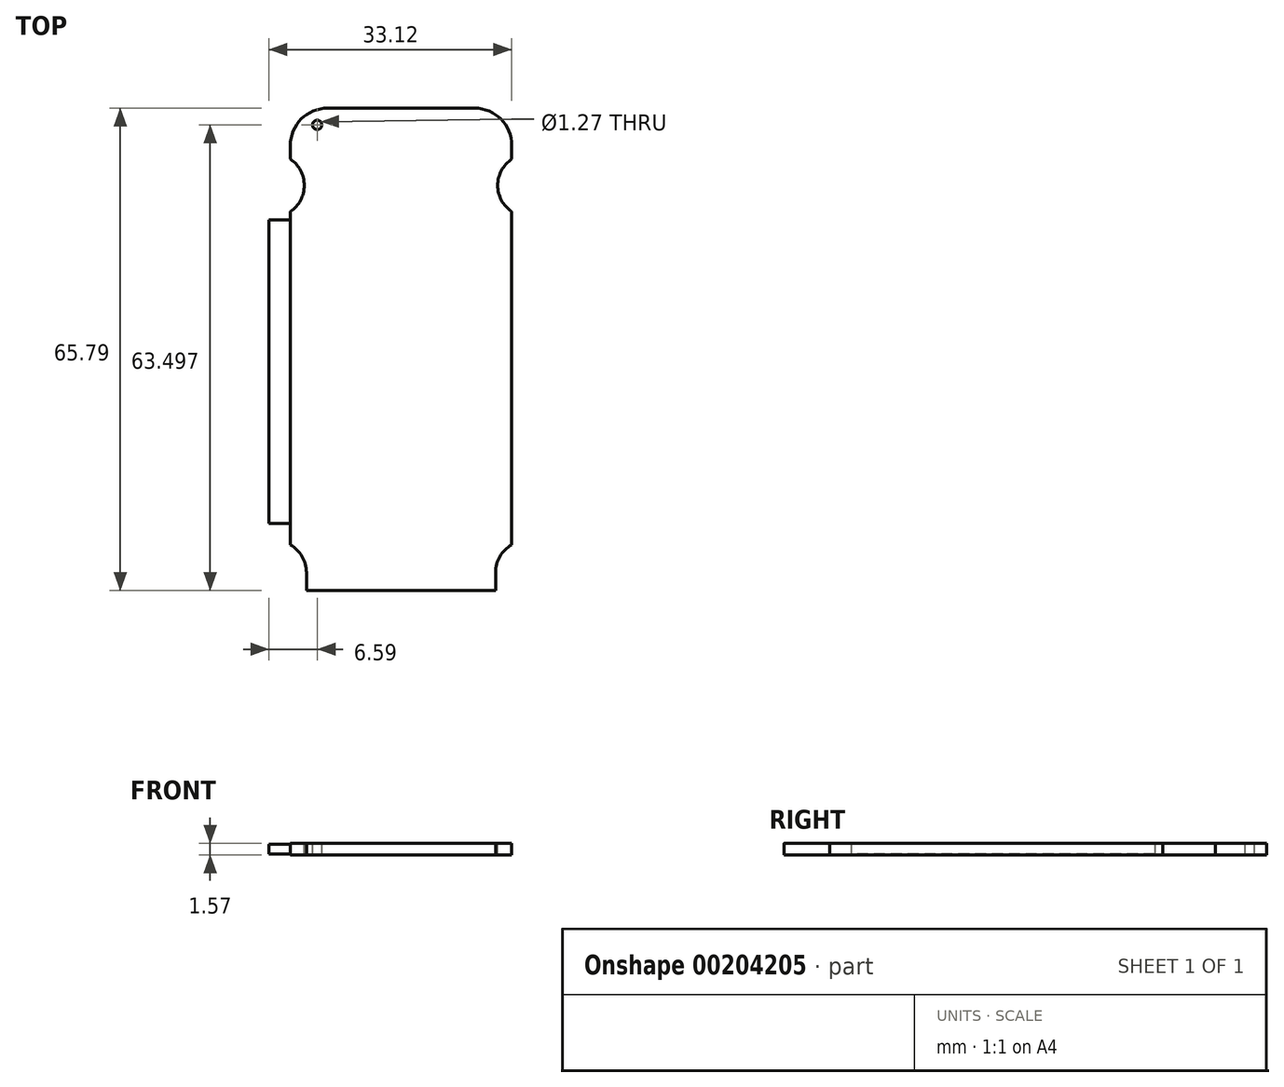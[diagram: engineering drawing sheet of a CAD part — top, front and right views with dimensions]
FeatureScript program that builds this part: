
annotation { "Feature Type Name" : "Feature", "Feature Type Description" : "" }
export const myFeature = defineFeature(function(context is Context, id is Id, definition is map)
    precondition{}
    {
        {
            var Q0;
            Q0=qCreatedBy(makeId("Top.planeOp"),FACE);
            var sketch = newSketch(context, id + "F0", { "sketchPlane" : qUnion([Q0])});
            skLineSegment(sketch, "E0.bottom", {"start": v(15.1, 28.5) * mm, "end": v(-15.1, 28.5) * mm});
            skLineSegment(sketch, "E0.top", {"start": v(15.1, -28.5) * mm, "end": v(-15.1, -28.5) * mm});
            skLineSegment(sketch, "E0.left", {"start": v(15.1, 28.5) * mm, "end": v(15.1, -28.5) * mm});
            skLineSegment(sketch, "E0.right", {"start": v(-15.1, 28.5) * mm, "end": v(-15.1, -28.5) * mm});
            skPoint(sketch, "E0.middle", {"position": v(0, 0) * mm});
            skSolve(sketch);
        }
        {
            var Q0;
            Q0=qSketchRegion(id+"F0",true);
            extrude(context, id + "F1", {"entities" : qUnion([Q0]), "depth" : 1.57 * mm});
        }
        {
            var Q0;
            Q0=makeQuery(id+"F1.opExtrude","SWEPT_FACE",FACE,{"disambiguationData":[OSD([sQuery(id+"F0.wireOp",EDGE,"E0.top")])]});
            var sketch = newSketch(context, id + "F2", { "sketchPlane" : qUnion([Q0])});
            skLineSegment(sketch, "E1.bottom", {"start": v(-15.1, 1.57) * mm, "end": v(15.1, 1.57) * mm});
            skLineSegment(sketch, "E1.top", {"start": v(-15.1, 0) * mm, "end": v(15.1, 0) * mm});
            skLineSegment(sketch, "E1.left", {"start": v(-15.1, 1.57) * mm, "end": v(-15.1, 0) * mm});
            skLineSegment(sketch, "E1.right", {"start": v(15.1, 1.57) * mm, "end": v(15.1, 0) * mm});
            skSolve(sketch);
        }
        {
            var Q0;
            Q0 = qSketchRegion(id + "F2", true);
            extrude(context, id + "F3", {"entities" : qUnion([Q0]), "operationType" : NewBodyOperationType.ADD, "depth" : 4.85 * mm + 2.03 * mm});
        }
        {
            var Q0;
            Q0=makeQuery(id+"F3.opExtrude","CAP_EDGE",EDGE,{"disambiguationData":[OSD([sQuery(id+"F2.wireOp",EDGE,"E1.right")])],"isStart":false});
            var Q1;
            Q1=makeQuery(id+"F3.opExtrude","CAP_EDGE",EDGE,{"disambiguationData":[OSD([sQuery(id+"F2.wireOp",EDGE,"E1.left")])],"isStart":false});
            fillet(context, id + "F4", {"entities" : qUnion([Q0, Q1]), "radius" : 2.54 * mm, "tangentPropagation" : true, "allowEdgeOverflow" : false});
        }
        {
            var Q0;
            Q0=makeQuery(id+"F3.boolean.opBoolean","MERGE",FACE,{"derivedFrom":[makeQuery(id+"F1.opExtrude","CAP_FACE",FACE,{"disambiguationData":[OSD([sQuery(id+"F0.wireOp",EDGE,"E0.bottom"),sQuery(id+"F0.wireOp",EDGE,"E0.top"),sQuery(id+"F0.wireOp",EDGE,"E0.left"),sQuery(id+"F0.wireOp",EDGE,"E0.right")])],"isStart":false}),makeQuery(id+"F3.opExtrude","SWEPT_FACE",FACE,{"disambiguationData":[OSD([sQuery(id+"F2.wireOp",EDGE,"E1.bottom")])]})]});
            var sketch = newSketch(context, id + "F5", { "sketchPlane" : qUnion([Q0])});
            skCircle(sketch, "E2", {"center": v(-17.51, 19.86) * mm, "radius": 4.33 * mm});
            skCircle(sketch, "E3", {"center": v(17.51, 19.86) * mm, "radius": 4.33 * mm});
            skCircle(sketch, "E4", {"center": v(-17.22, -32.92) * mm, "radius": 4.33 * mm});
            skCircle(sketch, "E5", {"center": v(17.22, -32.92) * mm, "radius": 4.33 * mm});
            skLineSegment(sketch, "E6", {"start": v(-17.22, -32.92) * mm, "end": v(17.22, -32.92) * mm, "construction": true});
            skLineSegment(sketch, "E7", {"start": v(0, -32.92) * mm, "end": v(0, 19.86) * mm, "construction": true});
            skLineSegment(sketch, "E8.bottom", {"start": v(-17.22, -32.92) * mm, "end": v(-12.9, -32.92) * mm});
            skLineSegment(sketch, "E8.top", {"start": v(-17.22, -37.25) * mm, "end": v(-12.9, -37.25) * mm});
            skLineSegment(sketch, "E8.left", {"start": v(-17.22, -32.92) * mm, "end": v(-17.22, -37.25) * mm});
            skLineSegment(sketch, "E8.right", {"start": v(-12.9, -32.92) * mm, "end": v(-12.9, -37.25) * mm});
            skLineSegment(sketch, "E9.bottom", {"start": v(17.22, -32.92) * mm, "end": v(12.9, -32.92) * mm});
            skLineSegment(sketch, "E9.top", {"start": v(17.22, -37.25) * mm, "end": v(12.9, -37.25) * mm});
            skLineSegment(sketch, "E9.left", {"start": v(17.22, -32.92) * mm, "end": v(17.22, -37.25) * mm});
            skLineSegment(sketch, "E9.right", {"start": v(12.9, -32.92) * mm, "end": v(12.9, -37.25) * mm});
            skLineSegment(sketch, "E10", {"start": v(-17.51, 19.86) * mm, "end": v(17.51, 19.86) * mm, "construction": true});
            skSolve(sketch);
        }
        {
            var Q0;
            Q0 = qSketchRegion(id + "F5", true);
            extrude(context, id + "F6", {"entities" : qUnion([Q0]), "operationType" : NewBodyOperationType.REMOVE, "endBound" : BoundingType.THROUGH_ALL, "oppositeDirection" : true, "depth" : 25.4 * mm});
        }
        {
            var Q0;
            Q0=makeQuery(id+"F1.opExtrude","SWEPT_FACE",FACE,{"disambiguationData":[OSD([sQuery(id+"F0.wireOp",EDGE,"E0.bottom")])]});
            var sketch = newSketch(context, id + "F7", { "sketchPlane" : qUnion([Q0])});
            skLineSegment(sketch, "E11.0", {"start": v(-15.1, 0) * mm, "end": v(15.1, 0) * mm});
            skLineSegment(sketch, "E12.0", {"start": v(15.1, 1.57) * mm, "end": v(15.1, 0) * mm});
            skLineSegment(sketch, "E13.0", {"start": v(-15.1, 1.57) * mm, "end": v(15.1, 1.57) * mm});
            skLineSegment(sketch, "E14.0", {"start": v(-15.1, 1.57) * mm, "end": v(-15.1, 0) * mm});
            skSolve(sketch);
        }
        {
            var Q0;
            Q0 = qSketchRegion(id + "F7", true);
            extrude(context, id + "F8", {"entities" : qUnion([Q0]), "operationType" : NewBodyOperationType.ADD, "depth" : 1.9 * mm});
        }
        {
            var Q0;
            Q0=makeQuery(id+"F8.opExtrude","CAP_EDGE",EDGE,{"disambiguationData":[OSD([sQuery(id+"F7.wireOp",EDGE,"E12.0")])],"isStart":false});
            var Q1;
            Q1=makeQuery(id+"F8.opExtrude","CAP_EDGE",EDGE,{"disambiguationData":[OSD([sQuery(id+"F7.wireOp",EDGE,"E14.0")])],"isStart":false});
            fillet(context, id + "F9", {"entities" : qUnion([Q0, Q1]), "radius" : 5.08 * mm, "tangentPropagation" : true, "allowEdgeOverflow" : false});
        }
        {
            var Q0;
            Q0=makeQuery(id+"F8.boolean.opBoolean","MERGE",FACE,{"derivedFrom":[makeQuery(id+"F3.boolean.opBoolean","MERGE",FACE,{"derivedFrom":[makeQuery(id+"F1.opExtrude","CAP_FACE",FACE,{"disambiguationData":[OSD([sQuery(id+"F0.wireOp",EDGE,"E0.bottom"),sQuery(id+"F0.wireOp",EDGE,"E0.top"),sQuery(id+"F0.wireOp",EDGE,"E0.left"),sQuery(id+"F0.wireOp",EDGE,"E0.right")])],"isStart":false}),makeQuery(id+"F3.opExtrude","SWEPT_FACE",FACE,{"disambiguationData":[OSD([sQuery(id+"F2.wireOp",EDGE,"E1.bottom")])]})]}),makeQuery(id+"F8.opExtrude","SWEPT_FACE",FACE,{"disambiguationData":[OSD([sQuery(id+"F7.wireOp",EDGE,"E13.0")])]})]});
            var sketch = newSketch(context, id + "F10", { "sketchPlane" : qUnion([Q0])});
            skCircle(sketch, "E15", {"center": v(-11.43, 28.12) * mm, "radius": 0.64 * mm});
            skSolve(sketch);
        }
        {
            var Q0;
            Q0 = qSketchRegion(id + "F10", true);
            extrude(context, id + "F11", {"entities" : qUnion([Q0]), "operationType" : NewBodyOperationType.REMOVE, "oppositeDirection" : true, "depth" : 25.4 * mm});
        }
        {
            var Q0;
            {var subQ0=sQuery(id+"F0.wireOp",EDGE,"E0.right");Q0=makeQuery(id+"F6.boolean.opBoolean","SPLIT",FACE,{"disambiguationData":[TD([makeQuery(id+"F6.opExtrude","SWEPT_FACE",FACE,{"disambiguationData":[OSD([sQuery(id+"F5.wireOp",EDGE,"E4")])]})])],"derivedFrom":makeQuery(id+"F3.boolean.opBoolean","MERGE",FACE,{"derivedFrom":[makeQuery(id+"F1.opExtrude","SWEPT_FACE",FACE,{"disambiguationData":[OSD([subQ0])]}),makeQuery(id+"F3.opExtrude","SWEPT_FACE",FACE,{"disambiguationData":[OSD([sQuery(id+"F2.wireOp",EDGE,"E1.left")])]})]})});}
            var sketch = newSketch(context, id + "F12", { "sketchPlane" : qUnion([Q0])});
            skLineSegment(sketch, "E16.bottom", {"start": v(-15.19, 1.45) * mm, "end": v(26.24, 1.45) * mm});
            skLineSegment(sketch, "E16.top", {"start": v(-15.19, 0.13) * mm, "end": v(26.24, 0.13) * mm});
            skLineSegment(sketch, "E16.left", {"start": v(-15.19, 1.45) * mm, "end": v(-15.19, 0.13) * mm});
            skLineSegment(sketch, "E16.right", {"start": v(26.24, 1.45) * mm, "end": v(26.24, 0.13) * mm});
            skSolve(sketch);
        }
        {
            var Q0;
            Q0 = qSketchRegion(id + "F12", true);
            extrude(context, id + "F13", {"entities" : qUnion([Q0]), "operationType" : NewBodyOperationType.ADD, "depth" : 2.92 * mm});
        }
    });
